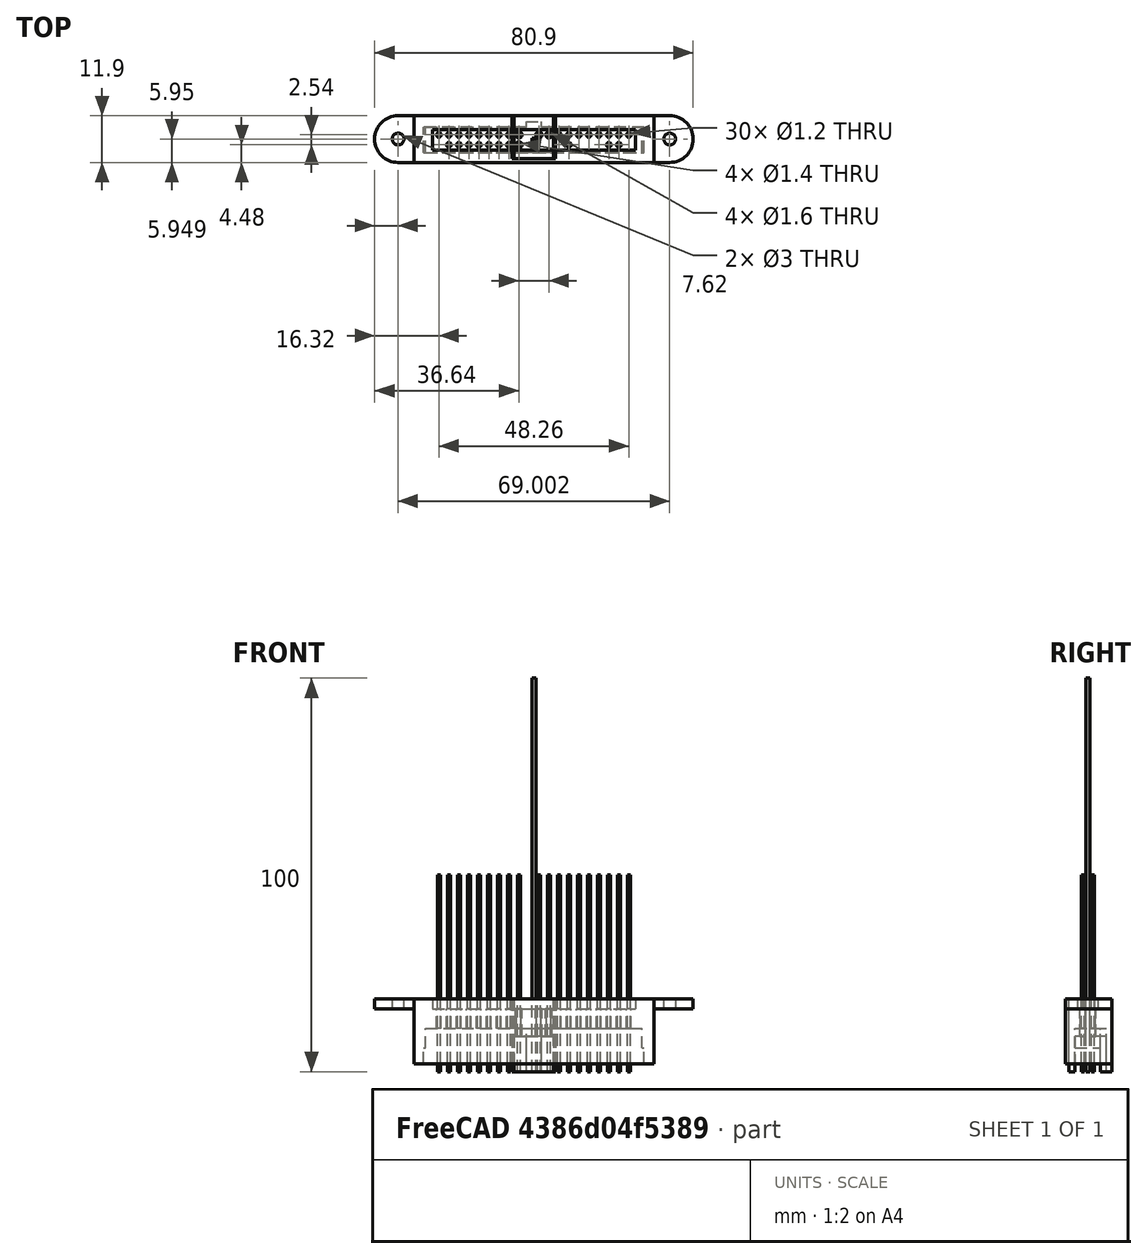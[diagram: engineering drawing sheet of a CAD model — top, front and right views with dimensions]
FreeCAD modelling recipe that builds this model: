
FCSTD DOCUMENT  (FreeCAD 0.18R4 (GitTag))
Label: pieza_ide
License: All rights reserved
LicenseURL: http://en.wikipedia.org/wiki/All_rights_reserved
objects: Part::Cut×32, Part::Box×26, Part::Cylinder×11, Sketcher::SketchObject×7, PartDesign::Pad×5, PartDesign::Body×5, Part::MultiFuse×5, Mesh::Feature×4, Part::Feature×3, Part::FeaturePython×2, PartDesign::Pocket×1, App::DocumentObjectGroup×1
note: 103 computed .brp shape members not serialized (recipe doc carries the construction recipe); baked Part::Feature solids carry a one-line shape summary decoded from their .brp

FEATURE [Sketcher::SketchObject] Sketch001  label="Sketch_ancho"
  MapMode = 5
  sketch-geometry (12):
    g0: LineSegment StartX=-28 StartY=-3.25 StartZ=0 EndX=-28 EndY=3.25 EndZ=0
    g1: LineSegment StartX=-28 StartY=3.25 StartZ=0 EndX=-1.9 EndY=3.25 EndZ=0
    g2: LineSegment StartX=-1.9 StartY=3.25 StartZ=0 EndX=-1.9 EndY=4.65 EndZ=0
    g3: LineSegment StartX=-1.9 StartY=4.65 StartZ=0 EndX=1.9 EndY=4.65 EndZ=0
    g4: LineSegment StartX=1.9 StartY=4.65 StartZ=0 EndX=1.9 EndY=3.25 EndZ=0
    g5: LineSegment StartX=1.9 StartY=3.25 StartZ=0 EndX=28 EndY=3.25 EndZ=0
    g6: LineSegment StartX=28 StartY=3.25 StartZ=0 EndX=28 EndY=-3.25 EndZ=0
    g7: LineSegment StartX=28 StartY=-3.25 StartZ=0 EndX=-28 EndY=-3.25 EndZ=0
    g8: LineSegment StartX=-29.5 StartY=6.15 StartZ=0 EndX=29.5 EndY=6.15 EndZ=0
    g9: LineSegment StartX=29.5 StartY=6.15 StartZ=0 EndX=29.5 EndY=-4.75 EndZ=0
    g10: LineSegment StartX=29.5 StartY=-4.75 StartZ=0 EndX=-29.5 EndY=-4.75 EndZ=0
    g11: LineSegment StartX=-29.5 StartY=-4.75 StartZ=0 EndX=-29.5 EndY=6.15 EndZ=0
  constraints (33):
    c: Coincident(g0,g1)
    c: Coincident(g1,g2)
    c: Coincident(g2,g3)
    c: Coincident(g3,g4)
    c: Coincident(g4,g5)
    c: Coincident(g5,g6)
    c: Coincident(g6,g7)
    c: Coincident(g7,g0)
    c: Vertical(g6)
    c: Vertical(g2)
    c: Vertical(g4)
    c: Horizontal(g1)
    c: Horizontal(g5)
    c: Horizontal(g4,g1)
    c: Coincident(g8,g9)
    c: Coincident(g9,g10)
    c: Coincident(g10,g11)
    c: Coincident(g11,g8)
    c: Horizontal(g8)
    c: Horizontal(g10)
    c: Vertical(g9)
    c: Vertical(g11)
    c: DistanceX(g7,g7) = 56
    c: DistanceY(g6,g6) = 6.5
    c: Symmetric(g2,g3,g-2)
    c: DistanceX(g3,g3) = 3.8
    c: Symmetric(g0,g0,g-1)
    c: Symmetric(g0,g6,g-2)
    c: DistanceY(g4,g4) = 1.4
    c: DistanceY(g2,g8) = 1.5
    c: DistanceY(g10,g0) = 1.5
    c: DistanceX(g6,g9) = 1.5
    c: DistanceX(g8,g0) = 1.5
FEATURE [PartDesign::Pad] Pad
  Length = 3
  Length2 = 100
  Profile = -> Sketch001
  Type = 0
FEATURE [PartDesign::Body] Body
  Group = -> [Pad]
  Origin = -> Origin
  Placement = pos=(0,0,-3) rot=(0,0,1;0rad)
  Tip = -> Pad
FEATURE [Sketcher::SketchObject] Sketch002  label="Sketch_angosto"
  MapMode = 5
  sketch-geometry (12):
    g0: LineSegment StartX=-27.5 StartY=-3.25 StartZ=0 EndX=-27.5 EndY=3.25 EndZ=0
    g1: LineSegment StartX=-27.5 StartY=3.25 StartZ=0 EndX=-1.9 EndY=3.25 EndZ=0
    g2: LineSegment StartX=-1.9 StartY=3.25 StartZ=0 EndX=-1.9 EndY=4.65 EndZ=0
    g3: LineSegment StartX=-1.9 StartY=4.65 StartZ=0 EndX=1.9 EndY=4.65 EndZ=0
    g4: LineSegment StartX=1.9 StartY=4.65 StartZ=0 EndX=1.9 EndY=3.25 EndZ=0
    g5: LineSegment StartX=1.9 StartY=3.25 StartZ=0 EndX=27.5 EndY=3.25 EndZ=0
    g6: LineSegment StartX=27.5 StartY=3.25 StartZ=0 EndX=27.5 EndY=-3.25 EndZ=0
    g7: LineSegment StartX=27.5 StartY=-3.25 StartZ=0 EndX=-27.5 EndY=-3.25 EndZ=0
    g8: LineSegment StartX=-29.5 StartY=6.15 StartZ=0 EndX=29.5 EndY=6.15 EndZ=0
    g9: LineSegment StartX=29.5 StartY=6.15 StartZ=0 EndX=29.5 EndY=-4.75 EndZ=0
    g10: LineSegment StartX=29.5 StartY=-4.75 StartZ=0 EndX=-29.5 EndY=-4.75 EndZ=0
    g11: LineSegment StartX=-29.5 StartY=-4.75 StartZ=0 EndX=-29.5 EndY=6.15 EndZ=0
  constraints (33):
    c: Coincident(g0,g1)
    c: Coincident(g1,g2)
    c: Coincident(g2,g3)
    c: Coincident(g3,g4)
    c: Coincident(g4,g5)
    c: Coincident(g5,g6)
    c: Coincident(g6,g7)
    c: Coincident(g7,g0)
    c: Vertical(g6)
    c: Vertical(g2)
    c: Vertical(g4)
    c: Horizontal(g1)
    c: Horizontal(g5)
    c: Horizontal(g4,g1)
    c: Coincident(g8,g9)
    c: Coincident(g9,g10)
    c: Coincident(g10,g11)
    c: Coincident(g11,g8)
    c: Horizontal(g8)
    c: Horizontal(g10)
    c: Vertical(g9)
    c: Vertical(g11)
    c: DistanceX(g7,g7) = 55
    c: DistanceY(g6,g6) = 6.5
    c: Symmetric(g2,g3,g-2)
    c: DistanceX(g3,g3) = 3.8
    c: Symmetric(g0,g0,g-1)
    c: Symmetric(g0,g6,g-2)
    c: DistanceY(g4,g4) = 1.4
    c: DistanceY(g2,g8) = 1.5
    c: DistanceY(g10,g0) = 1.5
    c: DistanceX(g6,g9) = 2
    c: DistanceX(g8,g0) = 2
FEATURE [PartDesign::Pad] Pad001
  Length = 6
  Length2 = 100
  Profile = -> Sketch002
  Type = 0
FEATURE [PartDesign::Body] Body001
  Group = -> [Pad001]
  Origin = -> Origin001
  Tip = -> Pad001
FEATURE [Sketcher::SketchObject] Sketch003  label="Sketch_cubo"
  MapMode = 5
  sketch-geometry (4):
    g0: LineSegment StartX=-29.5 StartY=6.15 StartZ=0 EndX=29.5 EndY=6.15 EndZ=0
    g1: LineSegment StartX=29.5 StartY=6.15 StartZ=0 EndX=29.5 EndY=-4.75 EndZ=0
    g2: LineSegment StartX=29.5 StartY=-4.75 StartZ=0 EndX=-29.5 EndY=-4.75 EndZ=0
    g3: LineSegment StartX=-29.5 StartY=-4.75 StartZ=0 EndX=-29.5 EndY=6.15 EndZ=0
  constraints (8):
    c: Coincident(g0,g1)
    c: Coincident(g1,g2)
    c: Coincident(g2,g3)
    c: Coincident(g3,g0)
    c: Horizontal(g0)
    c: Horizontal(g2)
    c: Vertical(g1)
    c: Vertical(g3)
FEATURE [PartDesign::Pad] Pad002
  Length = 9.5
  Length2 = 100
  Profile = -> Sketch003
  Type = 0
FEATURE [Sketcher::SketchObject] Sketch
  MapMode = 5
  Placement = pos=(0,0,9.5) rot=(0,0,1;0rad)
  Support = -> [Pad002]
  sketch-geometry (4):
    g0: LineSegment StartX=-25.75 StartY=2.6 StartZ=0 EndX=25.75 EndY=2.6 EndZ=0
    g1: LineSegment StartX=25.75 StartY=2.6 StartZ=0 EndX=25.75 EndY=-2.6 EndZ=0
    g2: LineSegment StartX=25.75 StartY=-2.6 StartZ=0 EndX=-25.75 EndY=-2.6 EndZ=0
    g3: LineSegment StartX=-25.75 StartY=-2.6 StartZ=0 EndX=-25.75 EndY=2.6 EndZ=0
  constraints (11):
    c: Coincident(g0,g1)
    c: Coincident(g1,g2)
    c: Coincident(g2,g3)
    c: Coincident(g3,g0)
    c: Horizontal(g0)
    c: Horizontal(g2)
    c: Vertical(g1)
    c: Vertical(g3)
    c: Symmetric(g0,g1,g-1)
    c: DistanceX(g0,g0) = 51.5
    c: DistanceY(g3,g3) = 5.2
FEATURE [PartDesign::Pocket] Pocket
  BaseFeature = -> Pad002
  Length = 2.5
  Length2 = 100
  Profile = -> Sketch
  Type = 0
FEATURE [PartDesign::Body] Body002
  Group = -> [Pad002,Sketch,Pocket]
  Origin = -> Origin002
  Placement = pos=(0,0,6) rot=(0,0,1;0rad)
  Tip = -> Pocket
FEATURE [Part::MultiFuse] Fusion  label="LosCuerposSinAgujeros"
  Shapes = -> [Body,Body001,Body002]
FEATURE [Part::Box] Box011  label="NuevoCuboCorte"
  AttacherType = Attacher::AttachEngine3D
  Height = 50
  Length = 1
  Placement = pos=(-24.63,-1.77,-3) rot=(0,0,1;0rad)
  Width = 1
FEATURE [Part::Box] Box012  label="Cube012"
  AttacherType = Attacher::AttachEngine3D
  Height = 50
  Length = 0.7
  Width = 0.7
FEATURE [Part::FeaturePython] Array001  label="NuevoArray"  # Draft array (typed FeaturePython)
  Angle = 360
  ArrayType = 0
  Axis = (0,0,1)
  Base = -> Box012
  Center = (0,0,0)
  Fuse = false
  IntervalAxis = (0,0,0)
  IntervalX = (2.54,0,0)
  IntervalY = (0,2.54,0)
  IntervalZ = (0,0,1)
  NumberPolar = 1
  NumberX = 20
  NumberY = 2
  NumberZ = 1
  Placement = pos=(-24.48,-1.62,-3) rot=(0,0,1;0rad)
FEATURE [Part::Box] Box013  label="CuboCentral"
  AttacherType = Attacher::AttachEngine3D
  Height = 100
  Length = 1
  Placement = pos=(-0.5,-0.5,-3) rot=(0,0,1;0rad)
  Width = 1
FEATURE [Part::Box] Box014  label="NuevoCuboCorte001"
  AttacherType = Attacher::AttachEngine3D
  Height = 50
  Length = 1
  Placement = pos=(-1.77,-1.77,-3) rot=(0,0,1;0rad)
  Width = 1
FEATURE [Part::Box] Box015  label="NuevoCuboCorte002"
  AttacherType = Attacher::AttachEngine3D
  Height = 50
  Length = 1
  Placement = pos=(0.77,-1.77,-3) rot=(0,0,1;0rad)
  Width = 1
FEATURE [Part::Box] Box016  label="NuevoCuboCorte003"
  AttacherType = Attacher::AttachEngine3D
  Height = 50
  Length = 1
  Placement = pos=(3.31,-1.77,-3) rot=(0,0,1;0rad)
  Width = 1
FEATURE [Part::Box] Box017  label="NuevoCuboCorte004"
  AttacherType = Attacher::AttachEngine3D
  Height = 50
  Length = 1
  Placement = pos=(5.85,-1.77,-3) rot=(0,0,1;0rad)
  Width = 1
FEATURE [Part::Box] Box018  label="NuevoCuboCorte005"
  AttacherType = Attacher::AttachEngine3D
  Height = 50
  Length = 1
  Placement = pos=(10.93,-1.77,-3) rot=(0,0,1;0rad)
  Width = 1
FEATURE [Part::Box] Box019  label="NuevoCuboCorte006"
  AttacherType = Attacher::AttachEngine3D
  Height = 50
  Length = 1
  Placement = pos=(13.47,-1.77,-3) rot=(0,0,1;0rad)
  Width = 1
FEATURE [Part::Box] Box020  label="NuevoCuboCorte007"
  AttacherType = Attacher::AttachEngine3D
  Height = 50
  Length = 1
  Placement = pos=(16.01,-1.77,-3) rot=(0,0,1;0rad)
  Width = 1
FEATURE [Part::Box] Box021  label="NuevoCuboCorte008"
  AttacherType = Attacher::AttachEngine3D
  Height = 50
  Length = 1
  Placement = pos=(23.63,-1.77,-3) rot=(0,0,1;0rad)
  Width = 1
FEATURE [Part::Box] Box022  label="NuevoCuboCorte009"
  AttacherType = Attacher::AttachEngine3D
  Height = 50
  Length = 1
  Placement = pos=(-1.77,0.77,-3) rot=(0,0,1;0rad)
  Width = 1
FEATURE [Part::Cut] Cut
  Base = -> Array001
  Tool = -> Box011
FEATURE [Part::Cut] Cut001
  Base = -> Cut
  Tool = -> Box014
FEATURE [Part::Cut] Cut002
  Base = -> Cut001
  Tool = -> Box015
FEATURE [Part::Cut] Cut003
  Base = -> Cut002
  Tool = -> Box016
FEATURE [Part::Cut] Cut004
  Base = -> Cut003
  Tool = -> Box017
FEATURE [Part::Cut] Cut005
  Base = -> Cut004
  Tool = -> Box018
FEATURE [Part::Cut] Cut006
  Base = -> Cut005
  Tool = -> Box019
FEATURE [Part::Cut] Cut007
  Base = -> Cut006
  Tool = -> Box020
FEATURE [Part::Cut] Cut008
  Base = -> Cut007
  Tool = -> Box021
FEATURE [Part::Cut] Cut009  label="dientes"
  Base = -> Cut008
  Tool = -> Box022
FEATURE [Sketcher::SketchObject] Sketch004  label="Sketch_pestania"
  MapMode = 5
  Placement = pos=(0,0,15.5) rot=(0,0,1;0rad)
  sketch-geometry (5):
    g0: LineSegment StartX=-29.5 StartY=6.15 StartZ=0 EndX=-32 EndY=6.15 EndZ=0
    g1: ArcOfCircle CenterX=-32 CenterY=0.7 CenterZ=0 NormalX=0 NormalY=0 NormalZ=1 AngleXU=0 Radius=5.45 StartAngle=1.5708 EndAngle=4.71239
    g2: LineSegment StartX=-32 StartY=-4.75 StartZ=0 EndX=-29.5 EndY=-4.75 EndZ=0
    g3: LineSegment StartX=-29.5 StartY=6.15 StartZ=0 EndX=-29.5 EndY=-4.75 EndZ=0
    g4: Circle CenterX=-31.9415 CenterY=0.665403 CenterZ=0 NormalX=0 NormalY=0 NormalZ=1 AngleXU=0 Radius=1.5
  constraints (8):
    c: Tangent(g0,g1) = -1.5708
    c: Tangent(g1,g2) = -1.5708
    c: Horizontal(g2)
    c: Horizontal(g0)
    c: DistanceX(g0,g0) = 2.5
    c: Coincident(g3,g0)
    c: Coincident(g3,g2)
    c: Radius(g4) = 1.5
FEATURE [Sketcher::SketchObject] Sketch009  label="Sketch009_pestania2"
  sketch-geometry (5):
    g0: LineSegment StartX=-32.8608 StartY=5.95 StartZ=0 EndX=-32.8608 EndY=-5.95 EndZ=0
    g1: LineSegment StartX=-32.8608 StartY=-5.95 StartZ=0 EndX=-36.8608 EndY=-5.95 EndZ=0
    g2: ArcOfCircle CenterX=-36.8608 CenterY=0 CenterZ=0 NormalX=0 NormalY=0 NormalZ=1 AngleXU=0 Radius=5.95 StartAngle=1.5708 EndAngle=4.71239
    g3: Circle CenterX=-36.8608 CenterY=0 CenterZ=0 NormalX=0 NormalY=0 NormalZ=1 AngleXU=0 Radius=1.5
    g4: LineSegment StartX=-32.8608 StartY=5.95 StartZ=0 EndX=-36.8608 EndY=5.95 EndZ=0
  constraints (13):
    c: Coincident(g0,g1)
    c: Tangent(g1,g2) = 1.5708
    c: Vertical(g0)
    c: DistanceY(g0,g0) = 11.9
    c: PointOnObject(g2,g-1)
    c: Radius(g3) = 1.5
    c: Coincident(g3,g2)
    c: Horizontal(g1)
    c: Equal(g4,g1)
    c: Coincident(g4,g0)
    c: Perpendicular(g0,g4)
    c: DistanceX(g4,g4) = 4
    c: Coincident(g2,g4)
FEATURE [App::DocumentObjectGroup] Group  label="sketches"
  Group = -> [Sketch001,Sketch002,Sketch003,Sketch004,Sketch009]
FEATURE [PartDesign::Pad] Pad007
  Length = 2.5
  Length2 = 100
  Profile = -> Sketch009
  Type = 0
FEATURE [PartDesign::Body] Body007  label="pestania2"
  Group = -> [Pad007]
  Origin = -> Origin007
  Placement = pos=(2.36,0.2,13) rot=(0,0,1;0rad)
  Tip = -> Pad007
FEATURE [Part::Cylinder] Cylinder
  Angle = 360
  AttacherType = Attacher::AttachEngine3D
  Height = 50
  Radius = 0.6
FEATURE [Part::FeaturePython] Array  # Draft array (typed FeaturePython)
  Angle = 360
  ArrayType = 0
  Axis = (0,0,1)
  Base = -> Cylinder
  Center = (0,0,0)
  Fuse = false
  IntervalAxis = (0,0,0)
  IntervalX = (2.54,0,0)
  IntervalY = (0,2.54,0)
  IntervalZ = (0,0,1)
  NumberPolar = 1
  NumberX = 20
  NumberY = 2
  NumberZ = 1
  Placement = pos=(-24.13,-1.27,0) rot=(0,0,1;0rad)
FEATURE [Part::Cylinder] Cylinder001  label="cilindro_tapa"
  Angle = 360
  AttacherType = Attacher::AttachEngine3D
  Height = 50
  Placement = pos=(-24.13,-1.27,0) rot=(0,0,1;0rad)
  Radius = 1.2
FEATURE [Part::Cylinder] Cylinder002  label="cilindro_tapa001"
  Angle = 360
  AttacherType = Attacher::AttachEngine3D
  Height = 50
  Placement = pos=(-1.27,-1.27,0) rot=(0,0,1;0rad)
  Radius = 1.2
FEATURE [Part::Cylinder] Cylinder003  label="cilindro_tapa002"
  Angle = 360
  AttacherType = Attacher::AttachEngine3D
  Height = 50
  Placement = pos=(-1.27,1.27,0) rot=(0,0,1;0rad)
  Radius = 1.2
FEATURE [Part::Cylinder] Cylinder004  label="cilindro_tapa003"
  Angle = 360
  AttacherType = Attacher::AttachEngine3D
  Height = 50
  Placement = pos=(1.27,-1.27,0) rot=(0,0,1;0rad)
  Radius = 1.2
FEATURE [Part::Cylinder] Cylinder005  label="cilindro_tapa004"
  Angle = 360
  AttacherType = Attacher::AttachEngine3D
  Height = 50
  Placement = pos=(3.81,-1.27,0) rot=(0,0,1;0rad)
  Radius = 1.2
FEATURE [Part::Cylinder] Cylinder006  label="cilindro_tapa005"
  Angle = 360
  AttacherType = Attacher::AttachEngine3D
  Height = 50
  Placement = pos=(6.35,-1.27,0) rot=(0,0,1;0rad)
  Radius = 1.2
FEATURE [Part::Cylinder] Cylinder007  label="cilindro_tapa006"
  Angle = 360
  AttacherType = Attacher::AttachEngine3D
  Height = 50
  Placement = pos=(11.43,-1.27,0) rot=(0,0,1;0rad)
  Radius = 1.2
FEATURE [Part::Cylinder] Cylinder008  label="cilindro_tapa007"
  Angle = 360
  AttacherType = Attacher::AttachEngine3D
  Height = 50
  Placement = pos=(13.97,-1.27,0) rot=(0,0,1;0rad)
  Radius = 1.2
FEATURE [Part::Cylinder] Cylinder009  label="cilindro_tapa008"
  Angle = 360
  AttacherType = Attacher::AttachEngine3D
  Height = 50
  Placement = pos=(16.51,-1.27,0) rot=(0,0,1;0rad)
  Radius = 1.2
FEATURE [Part::Cylinder] Cylinder010  label="cilindro_tapa009"
  Angle = 360
  AttacherType = Attacher::AttachEngine3D
  Height = 50
  Placement = pos=(24.13,-1.27,0) rot=(0,0,1;0rad)
  Radius = 1.2
FEATURE [Part::Cut] Cut010
  Base = -> Array
  Refine = true
  Tool = -> Cylinder001
FEATURE [Part::Cut] Cut011
  Base = -> Cut010
  Refine = true
  Tool = -> Cylinder010
FEATURE [Part::Cut] Cut012
  Base = -> Cut011
  Refine = true
  Tool = -> Cylinder009
FEATURE [Part::Cut] Cut013
  Base = -> Cut012
  Refine = true
  Tool = -> Cylinder008
FEATURE [Part::Cut] Cut014
  Base = -> Cut013
  Refine = true
  Tool = -> Cylinder007
FEATURE [Part::Cut] Cut015
  Base = -> Cut014
  Refine = true
  Tool = -> Cylinder006
FEATURE [Part::Cut] Cut016
  Base = -> Cut015
  Refine = true
  Tool = -> Cylinder005
FEATURE [Part::Cut] Cut017
  Base = -> Cut016
  Refine = true
  Tool = -> Cylinder004
FEATURE [Part::Cut] Cut018
  Base = -> Cut017
  Refine = true
  Tool = -> Cylinder003
FEATURE [Part::Cut] Cut019  label="dientes_redondos"
  Base = -> Cut018
  Refine = true
  Tool = -> Cylinder002
FEATURE [Part::Cut] Cut020  label="los_cuerpos_agujereados"
  Base = -> Fusion
  Refine = true
  Tool = -> Cut019
FEATURE [Part::Box] Box  label="Cube"
  AttacherType = Attacher::AttachEngine3D
  Height = 30
  Length = 50
  Placement = pos=(-55.5,-9,-9) rot=(0,0,1;0rad)
  Width = 20
FEATURE [Part::Box] Box023  label="Cube013"
  AttacherType = Attacher::AttachEngine3D
  Height = 30
  Length = 50
  Placement = pos=(5.5,-9,-9) rot=(0,0,1;0rad)
  Width = 20
FEATURE [Part::Box] Box024  label="Cube014"
  AttacherType = Attacher::AttachEngine3D
  Height = 30
  Length = 50
  Placement = pos=(5,-9,-9) rot=(0,0,1;0rad)
  Width = 20
FEATURE [Part::Box] Box025  label="Cube015"
  AttacherType = Attacher::AttachEngine3D
  Height = 30
  Length = 50
  Placement = pos=(-55,-9,-9) rot=(0,0,1;0rad)
  Width = 20
FEATURE [Part::Box] Box026  label="Cube016"
  AttacherType = Attacher::AttachEngine3D
  Height = 30
  Length = 50
  Placement = pos=(5,-9,-9) rot=(0,0,1;0rad)
  Width = 20
FEATURE [Part::Box] Box027  label="Cube017"
  AttacherType = Attacher::AttachEngine3D
  Height = 30
  Length = 50
  Placement = pos=(-55,-9,-9) rot=(0,0,1;0rad)
  Width = 20
FEATURE [Part::Feature] Fusion001001  label="soporte_ide001"
  shape: bbox 75.9 x 10.9 x 18.5 mm, 60 faces (baked)
FEATURE [Part::Cut] Cut021
  Base = -> Fusion001001
  Refine = true
  Tool = -> Box023
FEATURE [Part::Cut] Cut022  label="test_1.6"
  Base = -> Cut021
  Refine = true
  Tool = -> Box
FEATURE [Mesh::Feature] Mesh  label="test_1.6 (Meshed)"
FEATURE [Part::Feature] Fusion001002  label="soporte_ide002_14"
  shape: bbox 75.9 x 10.9 x 18.5 mm, 60 faces (baked)
FEATURE [Part::Feature] Fusion001003  label="soporte_ide002_12"
  shape: bbox 75.9 x 10.9 x 18.5 mm, 60 faces (baked)
FEATURE [Part::Cut] Cut023
  Base = -> Fusion001002
  Refine = true
  Tool = -> Box025
FEATURE [Part::Cut] Cut024  label="test_1.4"
  Base = -> Cut023
  Refine = true
  Tool = -> Box024
FEATURE [Part::Cut] Cut025
  Base = -> Fusion001003
  Refine = true
  Tool = -> Box027
FEATURE [Part::Cut] Cut026  label="test_1.2"
  Base = -> Cut025
  Refine = true
  Tool = -> Box026
FEATURE [Mesh::Feature] Mesh002  label="test_1.2 (Meshed)"
FEATURE [Mesh::Feature] Mesh003  label="test_1.4 (Meshed)"
FEATURE [Part::Box] Box028  label="Cube018"
  AttacherType = Attacher::AttachEngine3D
  Height = 18.5
  Length = 59
  Placement = pos=(-29.5,-5.75,-3) rot=(0,0,1;0rad)
  Width = 1
FEATURE [Part::MultiFuse] Fusion001004
  Refine = true
  Shapes = -> [Cut020,Box028]
FEATURE [Part::Box] Box029  label="Cube019"
  AttacherType = Attacher::AttachEngine3D
  Height = 18.5
  Length = 1
  Placement = pos=(-30.5,-5.75,-3) rot=(0,0,1;0rad)
  Width = 11.9
FEATURE [Part::Box] Box030  label="Cube020"
  AttacherType = Attacher::AttachEngine3D
  Height = 18.5
  Length = 1
  Placement = pos=(29.5,-5.75,-3) rot=(0,0,1;0rad)
  Width = 11.9
FEATURE [Part::MultiFuse] Fusion001005
  Refine = true
  Shapes = -> [Fusion001004,Box029]
FEATURE [Part::MultiFuse] Fusion001006  label="los_cuerpos_agujereados_reforzados"
  Refine = true
  Shapes = -> [Fusion001005,Box030]
FEATURE [Sketcher::SketchObject] Sketch011  label="Sketch009_pestania004"
  sketch-geometry (5):
    g0: LineSegment StartX=-32.8608 StartY=5.95 StartZ=0 EndX=-32.8608 EndY=-5.95 EndZ=0
    g1: LineSegment StartX=-32.8608 StartY=-5.95 StartZ=0 EndX=-36.8608 EndY=-5.95 EndZ=0
    g2: ArcOfCircle CenterX=-36.8608 CenterY=0 CenterZ=0 NormalX=0 NormalY=0 NormalZ=1 AngleXU=0 Radius=5.95 StartAngle=1.5708 EndAngle=4.71239
    g3: Circle CenterX=-36.8608 CenterY=0 CenterZ=0 NormalX=0 NormalY=0 NormalZ=1 AngleXU=0 Radius=1.5
    g4: LineSegment StartX=-32.8608 StartY=5.95 StartZ=0 EndX=-36.8608 EndY=5.95 EndZ=0
  constraints (13):
    c: Coincident(g0,g1)
    c: Tangent(g1,g2) = 1.5708
    c: Vertical(g0)
    c: DistanceY(g0,g0) = 11.9
    c: PointOnObject(g2,g-1)
    c: Radius(g3) = 1.5
    c: Coincident(g3,g2)
    c: Horizontal(g1)
    c: Equal(g4,g1)
    c: Coincident(g4,g0)
    c: Perpendicular(g0,g4)
    c: DistanceX(g4,g4) = 4
    c: Coincident(g2,g4)
FEATURE [PartDesign::Pad] Pad008
  Length = 2.5
  Length2 = 100
  Profile = -> Sketch011
  Type = 0
FEATURE [PartDesign::Body] Body008  label="pestania003"
  Group = -> [Pad008]
  Origin = -> Origin008
  Placement = pos=(-2.36,0.2,13) rot=(0,0,1;3.14159rad)
  Tip = -> Pad008
FEATURE [Part::MultiFuse] Fusion001007  label="pieza_ide_agujeros_1.2"
  Refine = true
  Shapes = -> [Fusion001006,Body007,Body008]
FEATURE [Part::Box] Box031  label="Cube021"
  AttacherType = Attacher::AttachEngine3D
  Height = 2
  Length = 55
  Placement = pos=(-27.5,-3.25,6) rot=(0,0,1;0rad)
  Width = 6.5
FEATURE [Part::Box] Box032  label="Cube022"
  AttacherType = Attacher::AttachEngine3D
  Height = 2
  Length = 3.8
  Placement = pos=(-1.9,3.25,6) rot=(0,0,1;0rad)
  Width = 1.4
FEATURE [Part::Cut] Cut027
  Base = -> Fusion001007
  Refine = true
  Tool = -> Box031
FEATURE [Part::Cut] Cut028
  Base = -> Cut027
  Refine = true
  Tool = -> Box032
FEATURE [Part::Box] Box033  label="Cube023"
  AttacherType = Attacher::AttachEngine3D
  Height = 3
  Length = 0.5
  Placement = pos=(27.5,-3.25,0) rot=(0,0,1;0rad)
  Width = 6.5
FEATURE [Part::Box] Box034  label="Cube024"
  AttacherType = Attacher::AttachEngine3D
  Height = 3
  Length = 0.5
  Placement = pos=(-28,-3.25,0) rot=(0,0,1;0rad)
  Width = 6.5
FEATURE [Part::Cut] Cut029
  Base = -> Cut028
  Refine = true
  Tool = -> Box033
FEATURE [Part::Cut] Cut030
  Base = -> Cut029
  Refine = true
  Tool = -> Box034
FEATURE [Part::Box] Box035  label="Cube025"
  AttacherType = Attacher::AttachEngine3D
  Height = 10
  Length = 70
  Placement = pos=(-35,-7,-11) rot=(0,0,1;0rad)
  Width = 15
FEATURE [Part::Cut] Cut031  label="pieza_ide_1.2_final"
  Base = -> Cut030
  Refine = true
  Tool = -> Box035
FEATURE [Mesh::Feature] Mesh004  label="pieza_ide_1.2_final (Meshed)"
